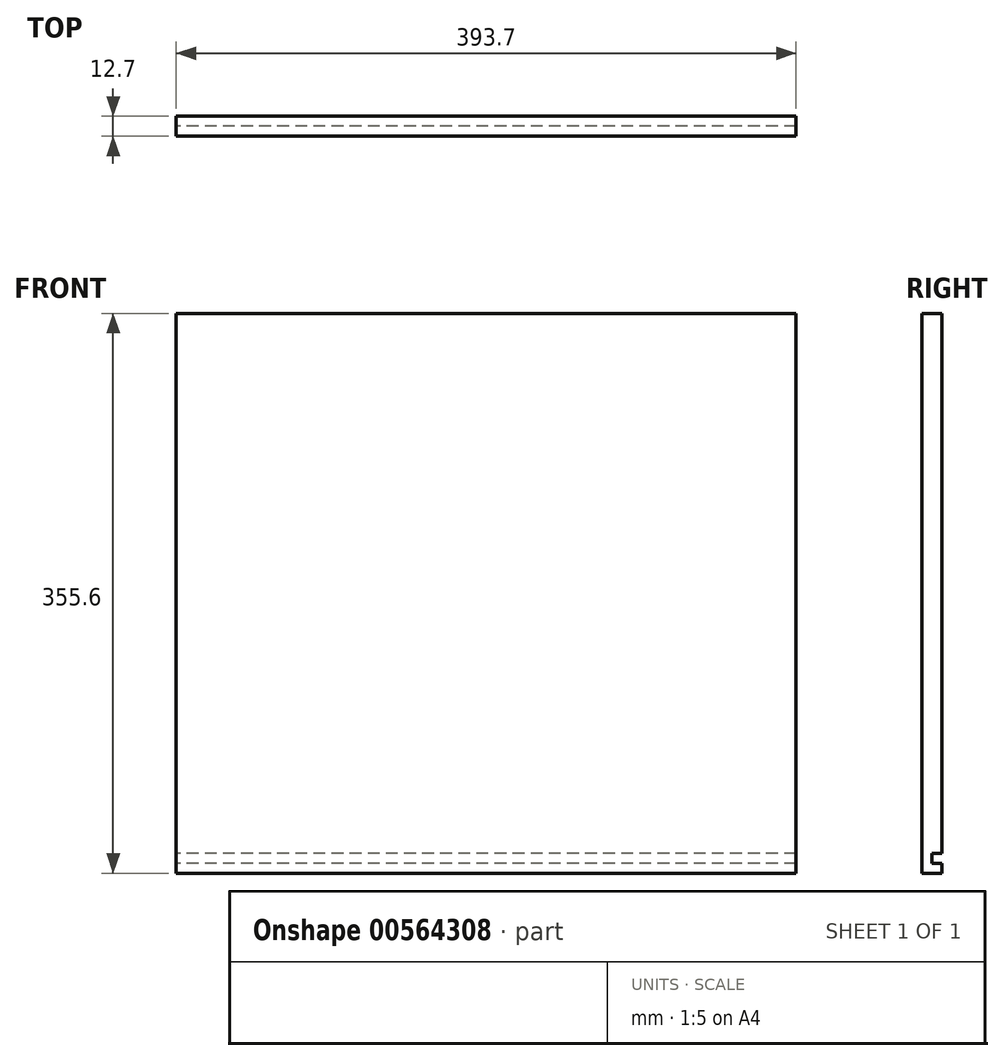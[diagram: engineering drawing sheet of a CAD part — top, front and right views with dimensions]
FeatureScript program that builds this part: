
annotation { "Feature Type Name" : "Feature", "Feature Type Description" : "" }
export const myFeature = defineFeature(function(context is Context, id is Id, definition is map)
    precondition{}
    {
        {
            var Q0;
            Q0=qCreatedBy(makeId("Front.planeOp"),FACE);
            var sketch = newSketch(context, id + "F0", { "sketchPlane" : qUnion([Q0])});
            skLineSegment(sketch, "E0.bottom", {"start": v(-196.85, 177.8) * mm, "end": v(196.85, 177.8) * mm});
            skLineSegment(sketch, "E0.top", {"start": v(-196.85, -177.8) * mm, "end": v(196.85, -177.8) * mm});
            skLineSegment(sketch, "E0.left", {"start": v(-196.85, 177.8) * mm, "end": v(-196.85, -177.8) * mm});
            skLineSegment(sketch, "E0.right", {"start": v(196.85, 177.8) * mm, "end": v(196.85, -177.8) * mm});
            skPoint(sketch, "E0.middle", {"position": v(0, 0) * mm});
            skSolve(sketch);
        }
        {
            var Q0;
            Q0 = qSketchRegion(id + "F0", true);
            var Q1;
            Q1=makeQuery(id+"F0.imprint","IMPRINT",FACE,{"disambiguationData":[TD([[makeQuery(id+"F0.imprint","IMPRINT",EDGE,{"derivedFrom":sQuery(id+"F0.wireOp",EDGE,"E0.bottom")}),-1.0]])]});
            extrude(context, id + "F1", {"entities" : qUnion([Q0, Q1]), "endBound" : BoundingType.SYMMETRIC, "depth" : 12.7 * mm, "offsetDistance" : 25.4 * mm});
        }
        {
            var Q0;
            Q0=makeQuery(id+"F1.opExtrude","CAP_FACE",FACE,{"disambiguationData":[OSD([sQuery(id+"F0.wireOp",EDGE,"E0.bottom"),sQuery(id+"F0.wireOp",EDGE,"E0.top"),sQuery(id+"F0.wireOp",EDGE,"E0.left"),sQuery(id+"F0.wireOp",EDGE,"E0.right")])],"isStart":true});
            var sketch = newSketch(context, id + "F2", { "sketchPlane" : qUnion([Q0])});
            skLineSegment(sketch, "E1.bottom", {"start": v(-196.85, -171.45) * mm, "end": v(196.85, -171.45) * mm});
            skLineSegment(sketch, "E1.top", {"start": v(-196.85, -165.1) * mm, "end": v(196.85, -165.1) * mm});
            skLineSegment(sketch, "E1.left", {"start": v(-196.85, -171.45) * mm, "end": v(-196.85, -165.1) * mm});
            skLineSegment(sketch, "E1.right", {"start": v(196.85, -171.45) * mm, "end": v(196.85, -165.1) * mm});
            skSolve(sketch);
        }
        {
            var Q0;
            Q0 = qSketchRegion(id + "F2", true);
            extrude(context, id + "F3", {"entities" : qUnion([Q0]), "operationType" : NewBodyOperationType.REMOVE, "oppositeDirection" : true, "depth" : 6.35 * mm, "offsetDistance" : 25.4 * mm});
        }
    });
